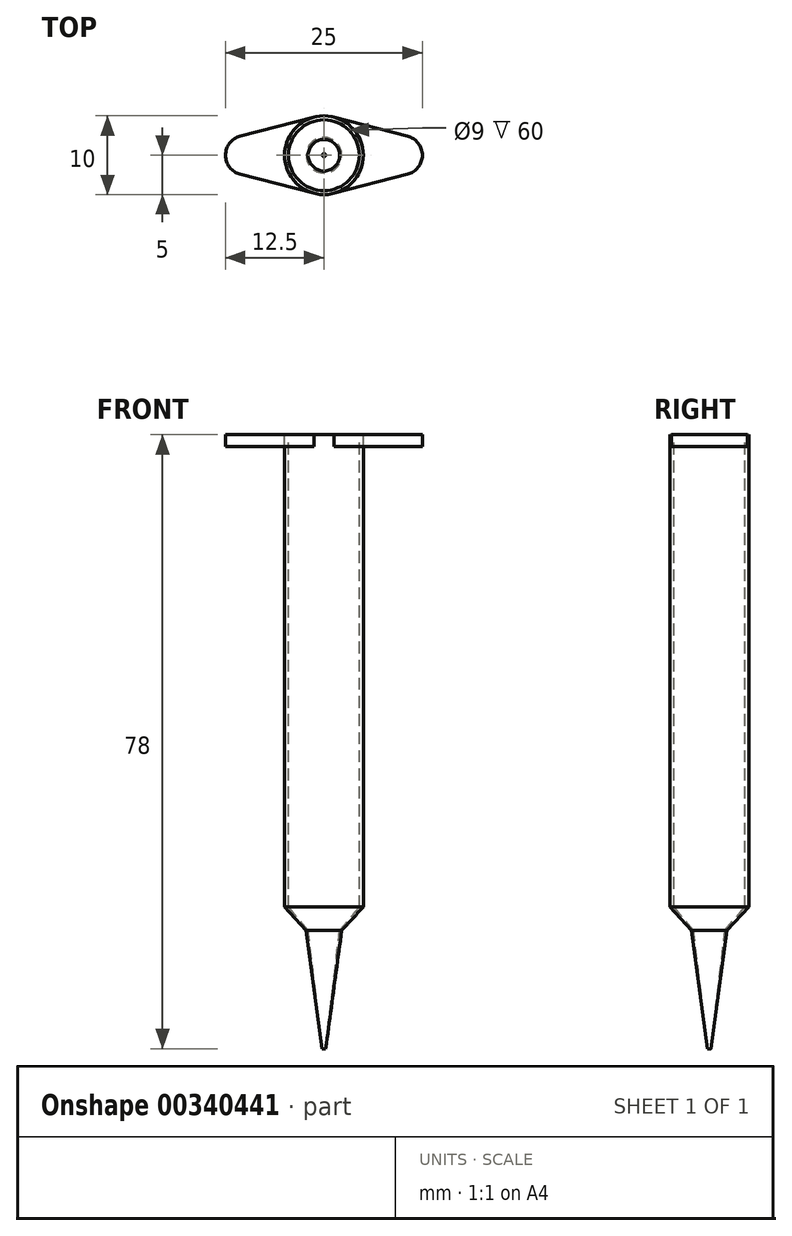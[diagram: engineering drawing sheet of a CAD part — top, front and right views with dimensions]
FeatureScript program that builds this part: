
annotation { "Feature Type Name" : "Feature", "Feature Type Description" : "" }
export const myFeature = defineFeature(function(context is Context, id is Id, definition is map)
    precondition{}
    {
        {
            var Q0;
            Q0=qCreatedBy(makeId("Top.planeOp"),FACE);
            var sketch = newSketch(context, id + "F0", { "sketchPlane" : qUnion([Q0])});
            skCircle(sketch, "E0", {"center": v(0, 0) * mm, "radius": 5 * mm});
            skCircle(sketch, "E1", {"center": v(0, 0) * mm, "radius": 4.5 * mm});
            skLineSegment(sketch, "E2", {"start": v(0, 0) * mm, "end": v(-10, 0) * mm});
            skLineSegment(sketch, "E3", {"start": v(0, 0) * mm, "end": v(10, 0) * mm});
            skLineSegment(sketch, "E4", {"start": v(-10.62, 2.42) * mm, "end": v(-1.25, 4.84) * mm});
            skLineSegment(sketch, "E5", {"start": v(-10.62, -2.42) * mm, "end": v(-1.25, -4.84) * mm});
            skLineSegment(sketch, "E6", {"start": v(1.25, 4.84) * mm, "end": v(10.63, 2.42) * mm});
            skLineSegment(sketch, "E7", {"start": v(1.25, -4.84) * mm, "end": v(10.62, -2.42) * mm});
            skArc(sketch, "E8", {"start": v(-10.62, 2.42) * mm, "mid": v(-12.5, 0) * mm, "end": v(-10.62, -2.42) * mm});
            skArc(sketch, "E9", {"start": v(10.63, 2.42) * mm, "mid": v(12.5, 0) * mm, "end": v(10.62, -2.42) * mm});
            skSolve(sketch);
        }
        {
            var Q0;
            {var subQ1=sQuery(id+"F0.wireOp",EDGE,"E4");Q0=makeQuery(id+"F0.imprint","IMPRINT",FACE,{"disambiguationData":[TD([[makeQuery(id+"F0.imprint","IMPRINT",EDGE,{"derivedFrom":subQ1}),-1.0]])]});}
            var Q1;
            {var subQ0=sQuery(id+"F0.wireOp",EDGE,"E6");Q1=makeQuery(id+"F0.imprint","IMPRINT",FACE,{"disambiguationData":[TD([[makeQuery(id+"F0.imprint","IMPRINT",EDGE,{"derivedFrom":subQ0}),-1.0]])]});}
            extrude(context, id + "F1", {"entities" : qUnion([Q0, Q1]), "oppositeDirection" : true, "depth" : 1.5 * mm});
        }
        {
            assignVariable(context, id + "F2", {"name" : "l1", "anyValue" : 60 * mm});
        }
        {
            var Q0;
            {var subQ5=sQuery(id+"F0.wireOp",EDGE,"E0");var subQ8=makeQuery(id+"F0.imprint","INTERSECT",VERTEX,{"derivedFrom":[subQ5,sQuery(id+"F0.wireOp",EDGE,"E5")]});Q0=makeQuery(id+"F0.imprint","IMPRINT",FACE,{"disambiguationData":[TD([[makeQuery(id+"F0.imprint","IMPRINT",EDGE,{"disambiguationData":[TD([[subQ8,1.0]])],"derivedFrom":subQ5}),1.0]])]});}
            var Q1;
            {var subQ0=sQuery(id+"F0.wireOp",EDGE,"E0");var subQ8=makeQuery(id+"F0.imprint","INTERSECT",VERTEX,{"derivedFrom":[subQ0,sQuery(id+"F0.wireOp",EDGE,"E6")]});Q1=makeQuery(id+"F0.imprint","IMPRINT",FACE,{"disambiguationData":[TD([[makeQuery(id+"F0.imprint","IMPRINT",EDGE,{"disambiguationData":[TD([[subQ8,1.0]])],"derivedFrom":subQ0}),1.0]])]});}
            extrude(context, id + "F3", {"entities" : qUnion([Q0, Q1]), "oppositeDirection" : true, "depth" : getVariable(context, 'l1')});
        }
        {
            assignVariable(context, id + "F4", {"name" : "l2", "anyValue" : 3 * mm});
        }
        {
            var Q0;
            Q0=qCreatedBy(makeId("Top.planeOp"),FACE);
            cPlane(context, id + "F5", {"entities" : qUnion([Q0]), "cplaneType" : CPlaneType.OFFSET, "offset" : getVariable(context, 'l1') + getVariable(context, 'l2'), "oppositeDirection" : true, "width" : 150 * mm, "height" : 150 * mm});
        }
        {
            var Q0;
            Q0=qCreatedBy(id+"F5.planeOp",FACE);
            var sketch = newSketch(context, id + "F6", { "sketchPlane" : qUnion([Q0])});
            skCircle(sketch, "E10", {"center": v(0, 0) * mm, "radius": 2 * mm});
            skCircle(sketch, "E11", {"center": v(0, 0) * mm, "radius": 2.25 * mm});
            skSolve(sketch);
        }
        {
            assignVariable(context, id + "F7", {"name" : "l3", "anyValue" : 15 * mm});
        }
        {
            var Q0;
            Q0=qCreatedBy(id+"F5.planeOp",FACE);
            cPlane(context, id + "F8", {"entities" : qUnion([Q0]), "cplaneType" : CPlaneType.OFFSET, "offset" : getVariable(context, 'l3'), "oppositeDirection" : true, "width" : 150 * mm, "height" : 150 * mm});
        }
        {
            var Q0;
            Q0=qCreatedBy(id+"F8.planeOp",FACE);
            var sketch = newSketch(context, id + "F9", { "sketchPlane" : qUnion([Q0])});
            skCircle(sketch, "E12", {"center": v(0, 0) * mm, "radius": 0.2 * mm});
            skCircle(sketch, "E13", {"center": v(0, 0) * mm, "radius": 0.23 * mm});
            skSolve(sketch);
        }
        {
            var Q0;
            Q0=qCreatedBy(makeId("Front.planeOp"),FACE);
            var sketch = newSketch(context, id + "F10", { "sketchPlane" : qUnion([Q0])});
            skLineSegment(sketch, "E14", {"start": v(-5, -60) * mm, "end": v(-2.25, -63) * mm});
            skLineSegment(sketch, "E15", {"start": v(-4.5, -60) * mm, "end": v(-2, -63) * mm});
            skLineSegment(sketch, "E16", {"start": v(5, -60) * mm, "end": v(2.25, -63) * mm});
            skLineSegment(sketch, "E17", {"start": v(4.5, -60) * mm, "end": v(2, -63) * mm});
            skLineSegment(sketch, "E18", {"start": v(-2.25, -63) * mm, "end": v(-0.23, -78) * mm});
            skLineSegment(sketch, "E19", {"start": v(-2, -63) * mm, "end": v(-0.2, -78) * mm});
            skLineSegment(sketch, "E20", {"start": v(2.25, -63) * mm, "end": v(0.23, -78) * mm});
            skLineSegment(sketch, "E21", {"start": v(2, -63) * mm, "end": v(0.2, -78) * mm});
            skLineSegment(sketch, "E22", {"start": v(0, -60) * mm, "end": v(0, -78) * mm});
            skLineSegment(sketch, "E23", {"start": v(-5, -60) * mm, "end": v(-4.5, -60) * mm});
            skLineSegment(sketch, "E24", {"start": v(-2.25, -63) * mm, "end": v(-2, -63) * mm});
            skLineSegment(sketch, "E25", {"start": v(2, -63) * mm, "end": v(2.25, -63) * mm});
            skLineSegment(sketch, "E26", {"start": v(4.5, -60) * mm, "end": v(5, -60) * mm});
            skLineSegment(sketch, "E27", {"start": v(-0.23, -78) * mm, "end": v(-0.2, -78) * mm});
            skLineSegment(sketch, "E28", {"start": v(0.2, -78) * mm, "end": v(0.23, -78) * mm});
            skSolve(sketch);
        }
        {
            var Q0;
            Q0=makeQuery(id+"F10.imprint","IMPRINT",FACE,{"disambiguationData":[TD([[makeQuery(id+"F10.imprint","IMPRINT",EDGE,{"derivedFrom":sQuery(id+"F10.wireOp",EDGE,"E14")}),1.0]])]});
            var Q1;
            Q1=sQuery(id+"F10.wireOp",EDGE,"E22");
            revolve(context, id + "F11", {"operationType" : NewBodyOperationType.ADD, "entities" : qUnion([Q0]), "axis" : qUnion([Q1]), "revolveType" : RevolveType.FULL});
        }
        {
            var Q0;
            Q0=makeQuery(id+"F10.imprint","IMPRINT",FACE,{"disambiguationData":[TD([[makeQuery(id+"F10.imprint","IMPRINT",EDGE,{"derivedFrom":sQuery(id+"F10.wireOp",EDGE,"E18")}),1.0]])]});
            var Q1;
            Q1=sQuery(id+"F10.wireOp",EDGE,"E22");
            revolve(context, id + "F12", {"operationType" : NewBodyOperationType.ADD, "entities" : qUnion([Q0]), "axis" : qUnion([Q1]), "revolveType" : RevolveType.FULL});
        }
    });
